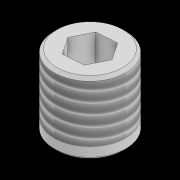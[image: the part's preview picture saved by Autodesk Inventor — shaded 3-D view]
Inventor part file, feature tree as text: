
AUTODESK INVENTOR PART (.ipt)
format: ipt  version: 2021 (Build 250183000, 183)  size: 118,784 bytes
history: native  units: mm
features: extrude x2, sketch x2, thread x1, chamfer x1
ambient origin geometry x8: Origin, YZ Plane, XZ Plane, XY Plane, X Axis, Y Axis, Z Axis, Center Point
bodies: Solid1 (feature_tree)
feature tree (6):
  extrude  "Extrusion1"  Depth=6.0mm
  extrude  "Extrusion2"  Depth=5.5mm TaperAngle=0.0deg
  thread  "Thread1"  [1 undecoded]
  chamfer  "Chamfer1"  Distance=0.5mm Angle=45.0deg
  sketch  "Sketch1"  dims[d0=12.0mm d1=0.0mm d2=6.0mm]
  sketch  "Sketch2"  dims[d3=12.0mm d4=5.5mm d5=0.0mm d6=10.0mm d7=0.0mm d8=0.5mm d9=2.0mm d10=45.0deg]
note: 1 required parameter value undecoded (feature->parameter linkage not recoverable at this tier; creation-order binding heuristic only, values carry confidence <= 0.55)
